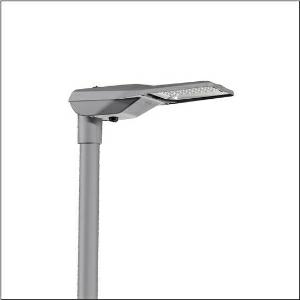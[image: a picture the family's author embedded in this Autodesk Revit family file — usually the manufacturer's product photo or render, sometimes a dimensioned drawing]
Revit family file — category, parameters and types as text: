
# Revit family: streetlight_sl_21_mini___st1_0a_5xe2d43t08jb_9874
name_source: partatom
category: Lighting Fixtures
units: mm (PartAtom-declared; Revit-internal decimal feet)

## family parameters
Cut with Voids When Loaded = No
Host = Face
Light Source = No
Part Type = Normal
Room Calculation Point = No
Round Connector Dimension = Use Diameter
Shared = No

## types (1)
- --- (1 x LED, 13500 lm, 88.6 W, 4000K)
    Apparent Load = 89 VA
    CIE Flux Codes = 40 73 97 100 100
    Color Rendering = 70
    Color Temperature = 4000K
    Default Elevation = 1800 mm
    Description = Streetlight SL 21 mini, mast luminaire, primary light control with lens, of PMMA, primary optical cover: cover, of toughened safety glass, transparent, light distribution: ST1.0a, light emission: direct distribution, primary light characteristic: asymmetric, installation type: side-entry, post-top, LED, High Power LED, rated luminous flux: 13.500lm, luminous efficacy: 152lm/W, light colour: 740, colour temperature: 4000K, control gear: D4i, control: overheat protection, constant luminous flux control, time-dependent luminous flux control, flexible luminous flux parameterisation, pre-setting: logarithmic dimming characteristic, mains connection: 220..240V, AC, 50/60Hz, start of lifetime: 89W, end of service life: 92W, reduction: 41W, luminaire housing, of diecast aluminium, powder-coated, SITECO metallic grey (DB 702S), corrosivity category C5 high according to DIN EN ISO 12944, please order mast flange separately, inclination adjustable: 0°, 5°, 10°, 15°, sealing non-destructively replaceable, multi-level sealing system, length: 628mm, width: 235mm, height: 110mm, mast flange for spigot size: 42mm (side-entry): 5XC10008XM4, 60/48mm (side-entry/post-top): 5XC10108XM2, 76/60mm (side-entry/post-top): 5XC10108XM1, mounting height: 4..8m, Smart Interface below and above, protection rating (complete): IP66, insulation class (complete): insulation class II (safety insulation), certification: CE, ENEC, ENEC+, VDE, impact resistance: IK10, permissible operating ambient temperature for outdoor applications: -40..+50°C, standard-compliant lighting for roads and squares, packaging unit: 1 piece

Light Distribution: ST1.0a
    Height = 110 mm
    Lamp = 1 x LED
    Lamp Light Flux = 13500 lm
    Lamp Power = 88.6 W
    Lamp count = 1
    Length = 625 mm
    Luminous efficacy = 152 lm/W
    Manufacturer = Siteco
    ModVariant = No
    Model = 5XE2D43T08JB
    Number of Poles = 1
    OnlyDefault = Yes
    Power Factor = 1
    Product Name = Streetlight SL 21 mini | ST1.0a
    Product group = mast luminaire | pylon top
    ProductGroupID = 6100
    Protection Class = Protection class II
    Protection Degree = IP 66
    RLX_Detail_Level = 1
    RLX_Emergency_Light_Flux = 0 lm
    RLX_Emergency_Type = 0
    RLX_Emergency_Type_DB = No
    RlxData = <blob elided: 26389 chars, md5=a4c0a73a>
    Socket = socket
    Standby Power = 0 W
    System Light Flux = 13500 lm
    System Power = 89 W
    Type Comments = factory setting: luminous flux: 100 % | dim-lin: 254 | 915 mA
    Type Image = l_1003514.jpg
    URL = http://relux.com
    VarID = @adj_031349
    Voltage = 0 V
    Weight = 0.00 kg
    Width = 234 mm

## geometry (parser evidence)
native form markers: Blend x4, Sweep x11
no freeform markers — native parametric forms only
